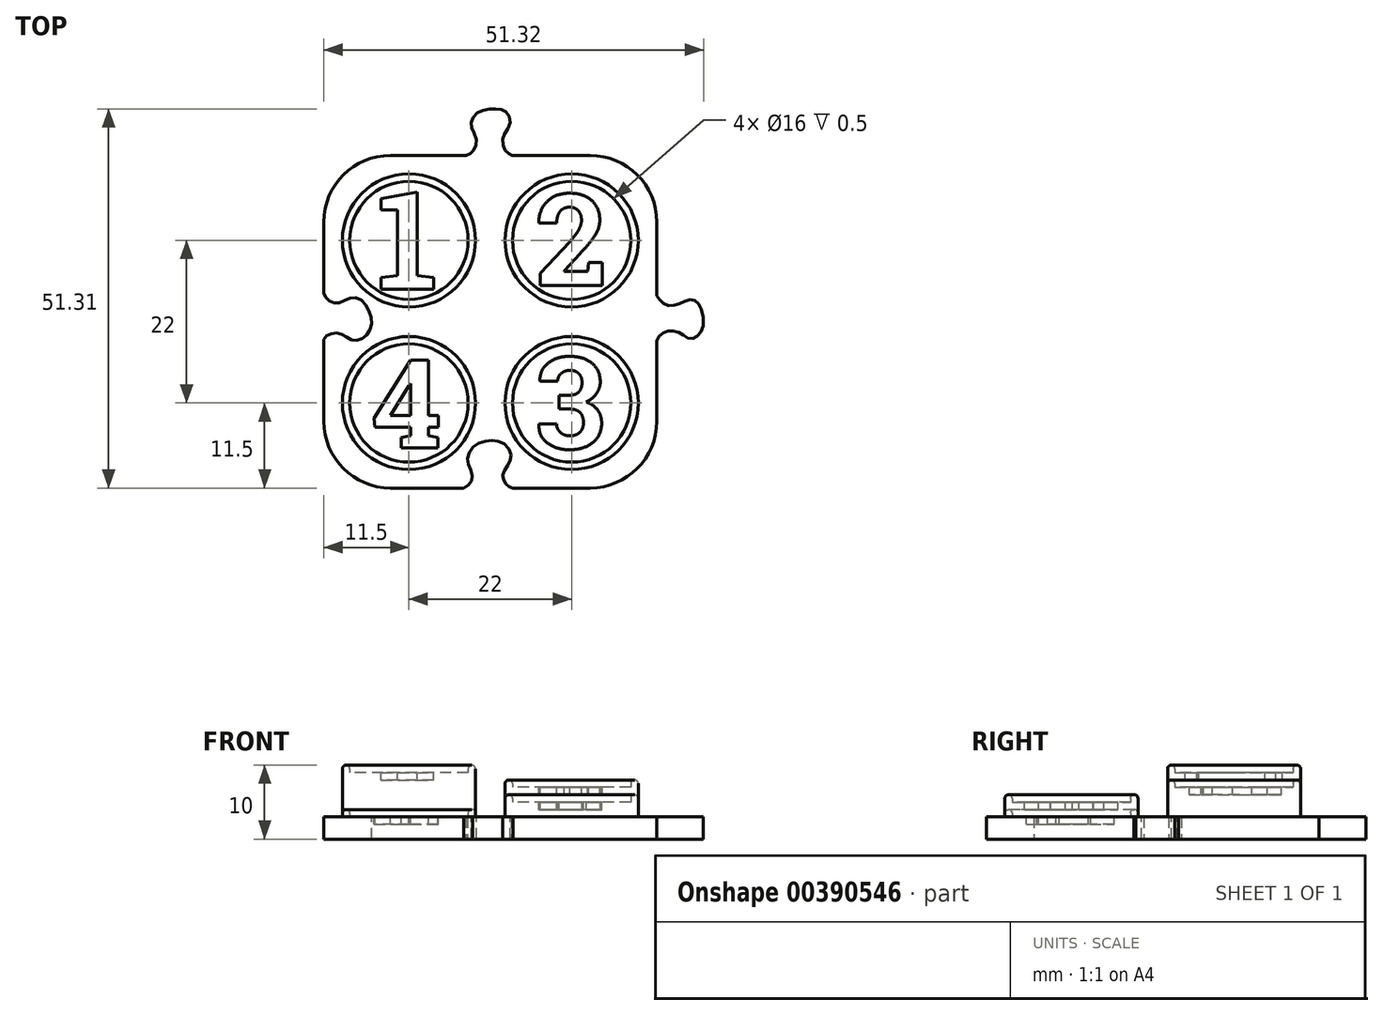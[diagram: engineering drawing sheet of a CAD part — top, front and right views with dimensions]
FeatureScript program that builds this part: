
annotation { "Feature Type Name" : "Feature", "Feature Type Description" : "" }
export const myFeature = defineFeature(function(context is Context, id is Id, definition is map)
    precondition{}
    {
        {
            var Q0;
            Q0=qCreatedBy(makeId("Top.planeOp"),FACE);
            var sketch = newSketch(context, id + "F0", { "sketchPlane" : qUnion([Q0])});
            skLineSegment(sketch, "E0.bottom", {"start": v(13.5, 13.5) * mm, "end": v(2.93, 13.5) * mm});
            skLineSegment(sketch, "E0.top", {"start": v(13.5, -13.5) * mm, "end": v(3.04, -13.5) * mm});
            skLineSegment(sketch, "E0.left", {"start": v(13.5, 13.5) * mm, "end": v(13.5, 3.49) * mm});
            skLineSegment(sketch, "E0.right", {"start": v(-13.5, 13.5) * mm, "end": v(-13.5, 3.89) * mm});
            skPoint(sketch, "E0.middle", {"position": v(0, 0) * mm});
            skFitSpline(sketch, "E1", {"points": [v(-13.5, -2.4) * mm, v(-13.06, -1.85) * mm, v(-12.19, -1.54) * mm, v(-11.23, -1.64) * mm, v(-10.18, -2.22) * mm, v(-9.3, -2.53) * mm, v(-8.23, -2.22) * mm, v(-7.52, -1.5) * mm, v(-7.03, -0.16) * mm, v(-7.37, 1.42) * mm, v(-8.21, 2.75) * mm, v(-9.3, 3.24) * mm, v(-10.53, 3) * mm, v(-11.5, 2.56) * mm, v(-12.42, 2.62) * mm, v(-13.18, 3.16) * mm, v(-13.5, 3.89) * mm], "startDerivative": vector(7.23, 11.93) * mm, "endDerivative": vector(-4.43, 14.21) * mm});
            skFitSpline(sketch, "E2", {"points": [v(-3.62, -13.5) * mm, v(-2.74, -12.9) * mm, v(-2.4, -12.05) * mm, v(-2.66, -11.08) * mm, v(-3.04, -10.02) * mm, v(-2.9, -8.8) * mm, v(-1.99, -7.67) * mm, v(-0.58, -7.14) * mm, v(0.76, -7.1) * mm, v(1.96, -7.62) * mm, v(2.79, -8.82) * mm, v(2.7, -9.8) * mm, v(2.12, -10.8) * mm, v(1.7, -11.65) * mm, v(1.76, -12.32) * mm, v(2.16, -13.02) * mm, v(2.6, -13.36) * mm, v(3.04, -13.5) * mm], "startDerivative": vector(16.2, 8.74) * mm, "endDerivative": vector(11.53, -2.8) * mm});
            skFitSpline(sketch, "E3", {"points": [v(-3.26, 13.5) * mm, v(-2.68, 13.76) * mm, v(-2.1, 14.46) * mm, v(-1.88, 15.61) * mm, v(-2.4, 17) * mm, v(-2.57, 17.9) * mm, v(-2.1, 18.93) * mm, v(-0.95, 19.6) * mm, v(0.43, 19.8) * mm, v(1.54, 19.7) * mm, v(2.37, 19.12) * mm, v(2.65, 17.8) * mm, v(2.02, 16.6) * mm, v(1.68, 15.55) * mm, v(1.92, 14.36) * mm, v(2.47, 13.75) * mm, v(2.93, 13.5) * mm], "startDerivative": vector(12.36, 4.01) * mm, "endDerivative": vector(10.48, -4.73) * mm});
            skFitSpline(sketch, "E4", {"points": [v(13.5, -2.57) * mm, v(13.97, -1.82) * mm, v(14.8, -1.34) * mm, v(15.69, -1.25) * mm, v(16.88, -1.66) * mm, v(17.63, -2.18) * mm, v(18.47, -2.24) * mm, v(19.2, -1.75) * mm, v(19.8, -0.34) * mm, v(19.4, 1.93) * mm, v(18.82, 2.75) * mm, v(18.04, 2.97) * mm, v(16.92, 2.58) * mm, v(15.97, 2.23) * mm, v(14.85, 2.24) * mm, v(13.98, 2.93) * mm, v(13.5, 3.49) * mm], "startDerivative": vector(6.76, 14.24) * mm, "endDerivative": vector(-8.43, 10.21) * mm});
            skLineSegment(sketch, "E5.trimOffspring", {"start": v(-3.26, 13.5) * mm, "end": v(-13.5, 13.5) * mm});
            skLineSegment(sketch, "E6.trimOffspring", {"start": v(13.5, -2.57) * mm, "end": v(13.5, -13.5) * mm});
            skLineSegment(sketch, "E7.trimOffspring", {"start": v(-3.62, -13.5) * mm, "end": v(-13.5, -13.5) * mm});
            skLineSegment(sketch, "E8.trimOffspring", {"start": v(-13.5, -2.4) * mm, "end": v(-13.5, -13.5) * mm});
            skPoint(sketch, "E9.visualSharp", {"position": v(-13.5, 13.5) * mm});
            skLineSegment(sketch, "E9.filletArc", {"start": v(-13.5, 13.5) * mm, "end": v(-13.5, 13.5) * mm});
            skPoint(sketch, "E10.visualSharp", {"position": v(13.5, 13.5) * mm});
            skLineSegment(sketch, "E10.filletArc", {"start": v(13.5, 13.5) * mm, "end": v(13.5, 13.5) * mm});
            skPoint(sketch, "E11.visualSharp", {"position": v(13.5, -13.5) * mm});
            skLineSegment(sketch, "E11.filletArc", {"start": v(13.5, -13.5) * mm, "end": v(13.5, -13.5) * mm});
            skPoint(sketch, "E12.visualSharp", {"position": v(-13.5, -13.5) * mm});
            skLineSegment(sketch, "E12.filletArc", {"start": v(-13.5, -13.5) * mm, "end": v(-13.5, -13.5) * mm});
            skLineSegment(sketch, "E13", {"start": v(-13.5, 4.5) * mm, "end": v(13.5, 4.5) * mm});
            skLineSegment(sketch, "E14", {"start": v(-4.5, 13.5) * mm, "end": v(-4.5, -13.5) * mm});
            skLineSegment(sketch, "E15", {"start": v(-13.5, -4.5) * mm, "end": v(13.5, -4.5) * mm});
            skLineSegment(sketch, "E16", {"start": v(4.5, 13.5) * mm, "end": v(4.5, -13.5) * mm});
            skSolve(sketch);
        }
        {
            var Q0;
            {var subQ1=sQuery(id+"F0.wireOp",EDGE,"E3");Q0=makeQuery(id+"F0.imprint","IMPRINT",FACE,{"disambiguationData":[TD([[makeQuery(id+"F0.imprint","IMPRINT",EDGE,{"derivedFrom":subQ1}),-1.0]])]});}
            var Q1;
            {var subQ0=sQuery(id+"F0.wireOp",EDGE,"E5.trimOffspring");var subQ1=sQuery(id+"F0.wireOp",EDGE,"E0.right");var subQ2=makeQuery(id+"F0.imprint","INTERSECT",VERTEX,{"derivedFrom":[subQ1,subQ0]});Q1=makeQuery(id+"F0.imprint","IMPRINT",FACE,{"disambiguationData":[TD([[makeQuery(id+"F0.imprint","IMPRINT",EDGE,{"disambiguationData":[TD([[subQ2,-1.0]])],"derivedFrom":subQ1}),1.0]])]});}
            var Q2;
            {var subQ0=sQuery(id+"F0.wireOp",EDGE,"E0.left");var subQ1=sQuery(id+"F0.wireOp",EDGE,"E0.bottom");var subQ2=makeQuery(id+"F0.imprint","INTERSECT",VERTEX,{"derivedFrom":[subQ1,subQ0]});Q2=makeQuery(id+"F0.imprint","IMPRINT",FACE,{"disambiguationData":[TD([[makeQuery(id+"F0.imprint","IMPRINT",EDGE,{"disambiguationData":[TD([[subQ2,-1.0]])],"derivedFrom":subQ1}),1.0]])]});}
            var Q3;
            {var subQ0=sQuery(id+"F0.wireOp",EDGE,"E14");var subQ1=sQuery(id+"F0.wireOp",EDGE,"E13");var subQ2=makeQuery(id+"F0.imprint","INTERSECT",VERTEX,{"derivedFrom":[subQ1,subQ0]});Q3=makeQuery(id+"F0.imprint","IMPRINT",FACE,{"disambiguationData":[TD([[makeQuery(id+"F0.imprint","IMPRINT",EDGE,{"disambiguationData":[TD([[subQ2,-1.0]])],"derivedFrom":subQ1}),-1.0]])]});}
            extrude(context, id + "F1", {"entities" : qUnion([Q0, Q1, Q2, Q3]), "depth" : 3 * mm});
        }
        {
            var Q0;
            {var subQ5=sQuery(id+"F0.wireOp",EDGE,"E4");Q0=makeQuery(id+"F0.imprint","IMPRINT",FACE,{"disambiguationData":[TD([[makeQuery(id+"F0.imprint","IMPRINT",EDGE,{"derivedFrom":subQ5}),1.0]])]});}
            var Q1;
            {var subQ0=sQuery(id+"F0.wireOp",EDGE,"E0.left");var subQ1=sQuery(id+"F0.wireOp",EDGE,"E0.bottom");var subQ2=makeQuery(id+"F0.imprint","INTERSECT",VERTEX,{"derivedFrom":[subQ1,subQ0]});Q1=makeQuery(id+"F0.imprint","IMPRINT",FACE,{"disambiguationData":[TD([[makeQuery(id+"F0.imprint","IMPRINT",EDGE,{"disambiguationData":[TD([[subQ2,-1.0]])],"derivedFrom":subQ1}),1.0]])]});}
            var Q2;
            {var subQ0=sQuery(id+"F0.wireOp",EDGE,"E6.trimOffspring");var subQ1=sQuery(id+"F0.wireOp",EDGE,"E0.top");var subQ2=makeQuery(id+"F0.imprint","INTERSECT",VERTEX,{"derivedFrom":[subQ1,subQ0]});Q2=makeQuery(id+"F0.imprint","IMPRINT",FACE,{"disambiguationData":[TD([[makeQuery(id+"F0.imprint","IMPRINT",EDGE,{"disambiguationData":[TD([[subQ2,-1.0]])],"derivedFrom":subQ1}),-1.0]])]});}
            var Q3;
            {var subQ0=sQuery(id+"F0.wireOp",EDGE,"E14");var subQ1=sQuery(id+"F0.wireOp",EDGE,"E13");var subQ2=makeQuery(id+"F0.imprint","INTERSECT",VERTEX,{"derivedFrom":[subQ1,subQ0]});Q3=makeQuery(id+"F0.imprint","IMPRINT",FACE,{"disambiguationData":[TD([[makeQuery(id+"F0.imprint","IMPRINT",EDGE,{"disambiguationData":[TD([[subQ2,-1.0]])],"derivedFrom":subQ1}),-1.0]])]});}
            extrude(context, id + "F2", {"entities" : qUnion([Q0, Q1, Q2, Q3]), "depth" : 3 * mm});
        }
        {
            var Q0;
            {var subQ5=sQuery(id+"F0.wireOp",EDGE,"E2");Q0=makeQuery(id+"F0.imprint","IMPRINT",FACE,{"disambiguationData":[TD([[makeQuery(id+"F0.imprint","IMPRINT",EDGE,{"derivedFrom":subQ5}),1.0]])]});}
            var Q1;
            {var subQ0=sQuery(id+"F0.wireOp",EDGE,"E8.trimOffspring");var subQ1=sQuery(id+"F0.wireOp",EDGE,"E7.trimOffspring");var subQ2=makeQuery(id+"F0.imprint","INTERSECT",VERTEX,{"derivedFrom":[subQ1,subQ0]});Q1=makeQuery(id+"F0.imprint","IMPRINT",FACE,{"disambiguationData":[TD([[makeQuery(id+"F0.imprint","IMPRINT",EDGE,{"disambiguationData":[TD([[subQ2,1.0]])],"derivedFrom":subQ1}),-1.0]])]});}
            var Q2;
            {var subQ0=sQuery(id+"F0.wireOp",EDGE,"E6.trimOffspring");var subQ1=sQuery(id+"F0.wireOp",EDGE,"E0.top");var subQ2=makeQuery(id+"F0.imprint","INTERSECT",VERTEX,{"derivedFrom":[subQ1,subQ0]});Q2=makeQuery(id+"F0.imprint","IMPRINT",FACE,{"disambiguationData":[TD([[makeQuery(id+"F0.imprint","IMPRINT",EDGE,{"disambiguationData":[TD([[subQ2,-1.0]])],"derivedFrom":subQ1}),-1.0]])]});}
            var Q3;
            {var subQ0=sQuery(id+"F0.wireOp",EDGE,"E14");var subQ1=sQuery(id+"F0.wireOp",EDGE,"E13");var subQ2=makeQuery(id+"F0.imprint","INTERSECT",VERTEX,{"derivedFrom":[subQ1,subQ0]});Q3=makeQuery(id+"F0.imprint","IMPRINT",FACE,{"disambiguationData":[TD([[makeQuery(id+"F0.imprint","IMPRINT",EDGE,{"disambiguationData":[TD([[subQ2,-1.0]])],"derivedFrom":subQ1}),-1.0]])]});}
            extrude(context, id + "F3", {"entities" : qUnion([Q0, Q1, Q2, Q3]), "depth" : 3 * mm});
        }
        {
            var Q0;
            {var subQ6=sQuery(id+"F0.wireOp",EDGE,"E1");Q0=makeQuery(id+"F0.imprint","IMPRINT",FACE,{"disambiguationData":[TD([[makeQuery(id+"F0.imprint","IMPRINT",EDGE,{"derivedFrom":subQ6}),-1.0]])]});}
            var Q1;
            {var subQ0=sQuery(id+"F0.wireOp",EDGE,"E5.trimOffspring");var subQ1=sQuery(id+"F0.wireOp",EDGE,"E0.right");var subQ2=makeQuery(id+"F0.imprint","INTERSECT",VERTEX,{"derivedFrom":[subQ1,subQ0]});Q1=makeQuery(id+"F0.imprint","IMPRINT",FACE,{"disambiguationData":[TD([[makeQuery(id+"F0.imprint","IMPRINT",EDGE,{"disambiguationData":[TD([[subQ2,-1.0]])],"derivedFrom":subQ1}),1.0]])]});}
            var Q2;
            {var subQ0=sQuery(id+"F0.wireOp",EDGE,"E8.trimOffspring");var subQ1=sQuery(id+"F0.wireOp",EDGE,"E7.trimOffspring");var subQ2=makeQuery(id+"F0.imprint","INTERSECT",VERTEX,{"derivedFrom":[subQ1,subQ0]});Q2=makeQuery(id+"F0.imprint","IMPRINT",FACE,{"disambiguationData":[TD([[makeQuery(id+"F0.imprint","IMPRINT",EDGE,{"disambiguationData":[TD([[subQ2,1.0]])],"derivedFrom":subQ1}),-1.0]])]});}
            var Q3;
            {var subQ0=sQuery(id+"F0.wireOp",EDGE,"E14");var subQ1=sQuery(id+"F0.wireOp",EDGE,"E13");var subQ2=makeQuery(id+"F0.imprint","INTERSECT",VERTEX,{"derivedFrom":[subQ1,subQ0]});Q3=makeQuery(id+"F0.imprint","IMPRINT",FACE,{"disambiguationData":[TD([[makeQuery(id+"F0.imprint","IMPRINT",EDGE,{"disambiguationData":[TD([[subQ2,-1.0]])],"derivedFrom":subQ1}),-1.0]])]});}
            extrude(context, id + "F4", {"entities" : qUnion([Q0, Q1, Q2, Q3]), "depth" : 3 * mm});
        }
        {
            var Q0;
            Q0=makeQuery(id+"F1.opExtrude","SWEPT_BODY",BODY,{"disambiguationData":[OSD([sQuery(id+"F0.wireOp",EDGE,"E0.bottom"),sQuery(id+"F0.wireOp",EDGE,"E0.left"),sQuery(id+"F0.wireOp",EDGE,"E0.right"),sQuery(id+"F0.wireOp",EDGE,"E3"),sQuery(id+"F0.wireOp",EDGE,"E5.trimOffspring"),sQuery(id+"F0.wireOp",EDGE,"E13"),sQuery(id+"F0.wireOp",EDGE,"E14"),sQuery(id+"F0.wireOp",EDGE,"E15"),sQuery(id+"F0.wireOp",EDGE,"E16")])]});
            transform(context, id + "F5", {"entities" : qUnion([Q0]), "transformType" : TransformType.TRANSLATION_3D, "dx" : 0 * mm, "dy" : 9 * mm, "dz" : 0 * mm, "makeCopy" : false});
        }
        {
            var Q0;
            Q0=makeQuery(id+"F2.opExtrude","SWEPT_BODY",BODY,{"disambiguationData":[OSD([sQuery(id+"F0.wireOp",EDGE,"E0.bottom"),sQuery(id+"F0.wireOp",EDGE,"E0.top"),sQuery(id+"F0.wireOp",EDGE,"E0.left"),sQuery(id+"F0.wireOp",EDGE,"E4"),sQuery(id+"F0.wireOp",EDGE,"E6.trimOffspring"),sQuery(id+"F0.wireOp",EDGE,"E13"),sQuery(id+"F0.wireOp",EDGE,"E14"),sQuery(id+"F0.wireOp",EDGE,"E15"),sQuery(id+"F0.wireOp",EDGE,"E16")])]});
            transform(context, id + "F6", {"entities" : qUnion([Q0]), "transformType" : TransformType.TRANSLATION_3D, "dx" : 9 * mm, "dy" : 0 * mm, "dz" : 0 * mm, "makeCopy" : false});
        }
        {
            var Q0;
            Q0=makeQuery(id+"F3.opExtrude","SWEPT_BODY",BODY,{"disambiguationData":[OSD([sQuery(id+"F0.wireOp",EDGE,"E0.top"),sQuery(id+"F0.wireOp",EDGE,"E2"),sQuery(id+"F0.wireOp",EDGE,"E6.trimOffspring"),sQuery(id+"F0.wireOp",EDGE,"E7.trimOffspring"),sQuery(id+"F0.wireOp",EDGE,"E8.trimOffspring"),sQuery(id+"F0.wireOp",EDGE,"E13"),sQuery(id+"F0.wireOp",EDGE,"E14"),sQuery(id+"F0.wireOp",EDGE,"E15"),sQuery(id+"F0.wireOp",EDGE,"E16")])]});
            transform(context, id + "F7", {"entities" : qUnion([Q0]), "transformType" : TransformType.TRANSLATION_3D, "dx" : 0 * mm, "dy" : -9 * mm, "dz" : 0 * mm, "makeCopy" : false});
        }
        {
            var Q0;
            Q0=makeQuery(id+"F4.opExtrude","SWEPT_BODY",BODY,{"disambiguationData":[OSD([sQuery(id+"F0.wireOp",EDGE,"E0.right"),sQuery(id+"F0.wireOp",EDGE,"E1"),sQuery(id+"F0.wireOp",EDGE,"E5.trimOffspring"),sQuery(id+"F0.wireOp",EDGE,"E7.trimOffspring"),sQuery(id+"F0.wireOp",EDGE,"E8.trimOffspring"),sQuery(id+"F0.wireOp",EDGE,"E13"),sQuery(id+"F0.wireOp",EDGE,"E14"),sQuery(id+"F0.wireOp",EDGE,"E15"),sQuery(id+"F0.wireOp",EDGE,"E16")])]});
            transform(context, id + "F8", {"entities" : qUnion([Q0]), "transformType" : TransformType.TRANSLATION_3D, "dx" : -9 * mm, "dy" : 0 * mm, "dz" : 0 * mm, "makeCopy" : false});
        }
        {
            var Q0;
            Q0=qCreatedBy(makeId("Top.planeOp"),FACE);
            var sketch = newSketch(context, id + "F9", { "sketchPlane" : qUnion([Q0])});
            skLineSegment(sketch, "E17.top", {"start": v(13.5, 22.5) * mm, "end": v(-13.5, 22.5) * mm});
            skLineSegment(sketch, "E17.left", {"start": v(22.5, -13.5) * mm, "end": v(22.5, 13.5) * mm});
            skPoint(sketch, "E18.visualSharp", {"position": v(22.5, 22.5) * mm});
            skArc(sketch, "E18.filletArc", {"start": v(22.5, 13.5) * mm, "mid": v(19.86, 19.86) * mm, "end": v(13.5, 22.5) * mm});
            skPoint(sketch, "E19.visualSharp", {"position": v(22.5, -22.5) * mm});
            skArc(sketch, "E19.filletArc", {"start": v(13.5, -22.5) * mm, "mid": v(19.86, -19.86) * mm, "end": v(22.5, -13.5) * mm});
            skPoint(sketch, "E20.visualSharp", {"position": v(-22.5, -22.5) * mm});
            skArc(sketch, "E20.filletArc", {"start": v(-22.5, -13.5) * mm, "mid": v(-19.86, -19.86) * mm, "end": v(-13.5, -22.5) * mm});
            skPoint(sketch, "E21.visualSharp", {"position": v(-22.5, 22.5) * mm});
            skArc(sketch, "E21.filletArc", {"start": v(-13.5, 22.5) * mm, "mid": v(-19.86, 19.86) * mm, "end": v(-22.5, 13.5) * mm});
            skLineSegment(sketch, "E22", {"start": v(-22.5, 13.5) * mm, "end": v(-12.08, 0) * mm});
            skLineSegment(sketch, "E23", {"start": v(-12.08, 0) * mm, "end": v(-22.5, -13.5) * mm});
            skLineSegment(sketch, "E24", {"start": v(-13.5, -22.5) * mm, "end": v(0, -11.74) * mm});
            skLineSegment(sketch, "E25", {"start": v(13.5, -22.5) * mm, "end": v(0, -11.74) * mm});
            skSolve(sketch);
        }
        {
            var Q0;
            Q0=qSketchRegion(id+"F9",true);
            extrude(context, id + "F10", {"entities" : qUnion([Q0]), "depth" : 3 * mm});
        }
        {
            var Q0;
            Q0=makeQuery(id+"F1.opExtrude","SWEPT_BODY",BODY,{"disambiguationData":[OSD([sQuery(id+"F0.wireOp",EDGE,"E0.bottom"),sQuery(id+"F0.wireOp",EDGE,"E0.left"),sQuery(id+"F0.wireOp",EDGE,"E0.right"),sQuery(id+"F0.wireOp",EDGE,"E3"),sQuery(id+"F0.wireOp",EDGE,"E5.trimOffspring"),sQuery(id+"F0.wireOp",EDGE,"E13"),sQuery(id+"F0.wireOp",EDGE,"E14"),sQuery(id+"F0.wireOp",EDGE,"E15"),sQuery(id+"F0.wireOp",EDGE,"E16")])]});
            var Q1;
            Q1=makeQuery(id+"F2.opExtrude","SWEPT_BODY",BODY,{"disambiguationData":[OSD([sQuery(id+"F0.wireOp",EDGE,"E0.bottom"),sQuery(id+"F0.wireOp",EDGE,"E0.top"),sQuery(id+"F0.wireOp",EDGE,"E0.left"),sQuery(id+"F0.wireOp",EDGE,"E4"),sQuery(id+"F0.wireOp",EDGE,"E6.trimOffspring"),sQuery(id+"F0.wireOp",EDGE,"E13"),sQuery(id+"F0.wireOp",EDGE,"E14"),sQuery(id+"F0.wireOp",EDGE,"E15"),sQuery(id+"F0.wireOp",EDGE,"E16")])]});
            var Q2;
            Q2=makeQuery(id+"F3.opExtrude","SWEPT_BODY",BODY,{"disambiguationData":[OSD([sQuery(id+"F0.wireOp",EDGE,"E0.top"),sQuery(id+"F0.wireOp",EDGE,"E2"),sQuery(id+"F0.wireOp",EDGE,"E6.trimOffspring"),sQuery(id+"F0.wireOp",EDGE,"E7.trimOffspring"),sQuery(id+"F0.wireOp",EDGE,"E8.trimOffspring"),sQuery(id+"F0.wireOp",EDGE,"E13"),sQuery(id+"F0.wireOp",EDGE,"E14"),sQuery(id+"F0.wireOp",EDGE,"E15"),sQuery(id+"F0.wireOp",EDGE,"E16")])]});
            var Q3;
            Q3=makeQuery(id+"F4.opExtrude","SWEPT_BODY",BODY,{"disambiguationData":[OSD([sQuery(id+"F0.wireOp",EDGE,"E0.right"),sQuery(id+"F0.wireOp",EDGE,"E1"),sQuery(id+"F0.wireOp",EDGE,"E5.trimOffspring"),sQuery(id+"F0.wireOp",EDGE,"E7.trimOffspring"),sQuery(id+"F0.wireOp",EDGE,"E8.trimOffspring"),sQuery(id+"F0.wireOp",EDGE,"E13"),sQuery(id+"F0.wireOp",EDGE,"E14"),sQuery(id+"F0.wireOp",EDGE,"E15"),sQuery(id+"F0.wireOp",EDGE,"E16")])]});
            var Q4;
            Q4=makeQuery(id+"F10.opExtrude","SWEPT_BODY",BODY,{"disambiguationData":[OSD([sQuery(id+"F9.wireOp",EDGE,"E17.top"),sQuery(id+"F9.wireOp",EDGE,"E17.left"),sQuery(id+"F9.wireOp",EDGE,"E18.filletArc"),sQuery(id+"F9.wireOp",EDGE,"E19.filletArc"),sQuery(id+"F9.wireOp",EDGE,"E20.filletArc"),sQuery(id+"F9.wireOp",EDGE,"E21.filletArc"),sQuery(id+"F9.wireOp",EDGE,"E22"),sQuery(id+"F9.wireOp",EDGE,"E23"),sQuery(id+"F9.wireOp",EDGE,"E24"),sQuery(id+"F9.wireOp",EDGE,"E25")])]});
            booleanBodies(context, id + "F11", {"operationType" : BooleanOperationType.UNION, "tools" : qUnion([Q0, Q1, Q2, Q3, Q4])});
        }
        {
            var Q0;
            {var subQ0=sQuery(id+"F0.wireOp",EDGE,"E16");var subQ1=sQuery(id+"F0.wireOp",EDGE,"E15");var subQ2=sQuery(id+"F0.wireOp",EDGE,"E14");var subQ3=sQuery(id+"F0.wireOp",EDGE,"E13");var subQ4=sQuery(id+"F0.wireOp",EDGE,"E8.trimOffspring");var subQ5=sQuery(id+"F0.wireOp",EDGE,"E7.trimOffspring");var subQ6=sQuery(id+"F0.wireOp",EDGE,"E5.trimOffspring");var subQ7=sQuery(id+"F0.wireOp",EDGE,"E0.right");var subQ8=sQuery(id+"F0.wireOp",EDGE,"E6.trimOffspring");var subQ9=sQuery(id+"F0.wireOp",EDGE,"E0.top");var subQ10=sQuery(id+"F0.wireOp",EDGE,"E0.left");var subQ11=sQuery(id+"F0.wireOp",EDGE,"E0.bottom");Q0=makeQuery(id+"F11.opBoolean","MERGE",FACE,{"derivedFrom":[makeQuery(id+"F1.opExtrude","CAP_FACE",FACE,{"disambiguationData":[OSD([subQ11,subQ10,subQ7,sQuery(id+"F0.wireOp",EDGE,"E3"),subQ6,subQ3,subQ2,subQ1,subQ0])],"isStart":false}),makeQuery(id+"F2.opExtrude","CAP_FACE",FACE,{"disambiguationData":[OSD([subQ11,subQ9,subQ10,sQuery(id+"F0.wireOp",EDGE,"E4"),subQ8,subQ3,subQ2,subQ1,subQ0])],"isStart":false}),makeQuery(id+"F3.opExtrude","CAP_FACE",FACE,{"disambiguationData":[OSD([subQ9,sQuery(id+"F0.wireOp",EDGE,"E2"),subQ8,subQ5,subQ4,subQ3,subQ2,subQ1,subQ0])],"isStart":false}),makeQuery(id+"F4.opExtrude","CAP_FACE",FACE,{"disambiguationData":[OSD([subQ7,sQuery(id+"F0.wireOp",EDGE,"E1"),subQ6,subQ5,subQ4,subQ3,subQ2,subQ1,subQ0])],"isStart":false}),makeQuery(id+"F10.opExtrude","CAP_FACE",FACE,{"disambiguationData":[OSD([sQuery(id+"F9.wireOp",EDGE,"E17.top"),sQuery(id+"F9.wireOp",EDGE,"E17.left"),sQuery(id+"F9.wireOp",EDGE,"E18.filletArc"),sQuery(id+"F9.wireOp",EDGE,"E19.filletArc"),sQuery(id+"F9.wireOp",EDGE,"E20.filletArc"),sQuery(id+"F9.wireOp",EDGE,"E21.filletArc"),sQuery(id+"F9.wireOp",EDGE,"E22"),sQuery(id+"F9.wireOp",EDGE,"E23"),sQuery(id+"F9.wireOp",EDGE,"E24"),sQuery(id+"F9.wireOp",EDGE,"E25")])],"isStart":false})]});}
            var sketch = newSketch(context, id + "F12", { "sketchPlane" : qUnion([Q0])});
            skLineSegment(sketch, "E26.bottom", {"start": v(11, -11) * mm, "end": v(-11, -11) * mm, "construction": true});
            skLineSegment(sketch, "E26.top", {"start": v(11, 11) * mm, "end": v(-11, 11) * mm, "construction": true});
            skLineSegment(sketch, "E26.left", {"start": v(11, -11) * mm, "end": v(11, 11) * mm, "construction": true});
            skLineSegment(sketch, "E26.right", {"start": v(-11, -11) * mm, "end": v(-11, 11) * mm, "construction": true});
            skPoint(sketch, "E26.middle", {"position": v(0, 0) * mm});
            skCircle(sketch, "E27", {"center": v(-11, 11) * mm, "radius": 9 * mm});
            skCircle(sketch, "E28", {"center": v(11, 11) * mm, "radius": 9 * mm});
            skCircle(sketch, "E29", {"center": v(11, -11) * mm, "radius": 9 * mm});
            skCircle(sketch, "E30", {"center": v(-11, -11) * mm, "radius": 9 * mm});
            skCircle(sketch, "E31", {"center": v(-11, 11) * mm, "radius": 8 * mm});
            skCircle(sketch, "E32", {"center": v(11, 11) * mm, "radius": 8 * mm});
            skCircle(sketch, "E33", {"center": v(11, -11) * mm, "radius": 8 * mm});
            skCircle(sketch, "E34", {"center": v(-11, -11) * mm, "radius": 8 * mm});
            skSolve(sketch);
        }
        {
            var Q0;
            Q0=makeQuery(id+"F12.imprint","IMPRINT",FACE,{"disambiguationData":[TD([[makeQuery(id+"F12.imprint","IMPRINT",EDGE,{"derivedFrom":sQuery(id+"F12.wireOp",EDGE,"E27")}),1.0]])]});
            extrude(context, id + "F13", {"entities" : qUnion([Q0]), "operationType" : NewBodyOperationType.ADD, "depth" : 7 * mm});
        }
        {
            var Q0;
            {var subQ0=sQuery(id+"F0.wireOp",EDGE,"E16");var subQ1=sQuery(id+"F0.wireOp",EDGE,"E15");var subQ2=sQuery(id+"F0.wireOp",EDGE,"E14");var subQ3=sQuery(id+"F0.wireOp",EDGE,"E13");var subQ4=sQuery(id+"F0.wireOp",EDGE,"E8.trimOffspring");var subQ5=sQuery(id+"F0.wireOp",EDGE,"E7.trimOffspring");var subQ6=sQuery(id+"F0.wireOp",EDGE,"E5.trimOffspring");var subQ7=sQuery(id+"F0.wireOp",EDGE,"E0.right");var subQ8=sQuery(id+"F0.wireOp",EDGE,"E6.trimOffspring");var subQ9=sQuery(id+"F0.wireOp",EDGE,"E0.top");var subQ10=sQuery(id+"F0.wireOp",EDGE,"E0.left");var subQ11=sQuery(id+"F0.wireOp",EDGE,"E0.bottom");Q0=makeQuery(id+"F13.boolean.opBoolean","SPLIT",FACE,{"disambiguationData":[TD([makeQuery(id+"F13.opExtrude","SWEPT_FACE",FACE,{"disambiguationData":[OSD([sQuery(id+"F12.wireOp",EDGE,"E31")])]})])],"derivedFrom":makeQuery(id+"F11.opBoolean","MERGE",FACE,{"derivedFrom":[makeQuery(id+"F1.opExtrude","CAP_FACE",FACE,{"disambiguationData":[OSD([subQ11,subQ10,subQ7,sQuery(id+"F0.wireOp",EDGE,"E3"),subQ6,subQ3,subQ2,subQ1,subQ0])],"isStart":false}),makeQuery(id+"F2.opExtrude","CAP_FACE",FACE,{"disambiguationData":[OSD([subQ11,subQ9,subQ10,sQuery(id+"F0.wireOp",EDGE,"E4"),subQ8,subQ3,subQ2,subQ1,subQ0])],"isStart":false}),makeQuery(id+"F3.opExtrude","CAP_FACE",FACE,{"disambiguationData":[OSD([subQ9,sQuery(id+"F0.wireOp",EDGE,"E2"),subQ8,subQ5,subQ4,subQ3,subQ2,subQ1,subQ0])],"isStart":false}),makeQuery(id+"F4.opExtrude","CAP_FACE",FACE,{"disambiguationData":[OSD([subQ7,sQuery(id+"F0.wireOp",EDGE,"E1"),subQ6,subQ5,subQ4,subQ3,subQ2,subQ1,subQ0])],"isStart":false}),makeQuery(id+"F10.opExtrude","CAP_FACE",FACE,{"disambiguationData":[OSD([sQuery(id+"F9.wireOp",EDGE,"E17.top"),sQuery(id+"F9.wireOp",EDGE,"E17.left"),sQuery(id+"F9.wireOp",EDGE,"E18.filletArc"),sQuery(id+"F9.wireOp",EDGE,"E19.filletArc"),sQuery(id+"F9.wireOp",EDGE,"E20.filletArc"),sQuery(id+"F9.wireOp",EDGE,"E21.filletArc"),sQuery(id+"F9.wireOp",EDGE,"E22"),sQuery(id+"F9.wireOp",EDGE,"E23"),sQuery(id+"F9.wireOp",EDGE,"E24"),sQuery(id+"F9.wireOp",EDGE,"E25")])],"isStart":false})]})});}
            extrude(context, id + "F14", {"entities" : qUnion([Q0]), "operationType" : NewBodyOperationType.ADD, "depth" : 6 * mm});
        }
        {
            var Q0;
            Q0=makeQuery(id+"F12.imprint","IMPRINT",FACE,{"disambiguationData":[TD([[makeQuery(id+"F12.imprint","IMPRINT",EDGE,{"derivedFrom":sQuery(id+"F12.wireOp",EDGE,"E28")}),1.0]])]});
            extrude(context, id + "F15", {"entities" : qUnion([Q0]), "operationType" : NewBodyOperationType.ADD, "depth" : 5 * mm});
        }
        {
            var Q0;
            Q0=makeQuery(id+"F12.imprint","IMPRINT",FACE,{"disambiguationData":[TD([[makeQuery(id+"F12.imprint","IMPRINT",EDGE,{"derivedFrom":sQuery(id+"F12.wireOp",EDGE,"E32")}),1.0]])]});
            extrude(context, id + "F16", {"entities" : qUnion([Q0]), "operationType" : NewBodyOperationType.ADD, "depth" : 4 * mm});
        }
        {
            var Q0;
            Q0=makeQuery(id+"F12.imprint","IMPRINT",FACE,{"disambiguationData":[TD([[makeQuery(id+"F12.imprint","IMPRINT",EDGE,{"derivedFrom":sQuery(id+"F12.wireOp",EDGE,"E29")}),1.0]])]});
            extrude(context, id + "F17", {"entities" : qUnion([Q0]), "operationType" : NewBodyOperationType.ADD, "depth" : 3 * mm});
        }
        {
            var Q0;
            Q0=makeQuery(id+"F12.imprint","IMPRINT",FACE,{"disambiguationData":[TD([[makeQuery(id+"F12.imprint","IMPRINT",EDGE,{"derivedFrom":sQuery(id+"F12.wireOp",EDGE,"E33")}),1.0]])]});
            extrude(context, id + "F18", {"entities" : qUnion([Q0]), "operationType" : NewBodyOperationType.ADD, "depth" : 2 * mm});
        }
        {
            var Q0;
            Q0=makeQuery(id+"F12.imprint","IMPRINT",FACE,{"disambiguationData":[TD([[makeQuery(id+"F12.imprint","IMPRINT",EDGE,{"derivedFrom":sQuery(id+"F12.wireOp",EDGE,"E30")}),1.0]])]});
            extrude(context, id + "F19", {"entities" : qUnion([Q0]), "operationType" : NewBodyOperationType.ADD, "depth" : 1 * mm});
        }
        {
            var Q0;
            Q0=makeQuery(id+"F14.opExtrude","CAP_FACE",FACE,{"disambiguationData":[OSD([sQuery(id+"F0.wireOp",EDGE,"E0.bottom"),sQuery(id+"F0.wireOp",EDGE,"E0.top"),sQuery(id+"F0.wireOp",EDGE,"E0.left"),sQuery(id+"F0.wireOp",EDGE,"E0.right"),sQuery(id+"F0.wireOp",EDGE,"E1"),sQuery(id+"F0.wireOp",EDGE,"E2"),sQuery(id+"F0.wireOp",EDGE,"E3"),sQuery(id+"F0.wireOp",EDGE,"E4"),sQuery(id+"F0.wireOp",EDGE,"E5.trimOffspring"),sQuery(id+"F0.wireOp",EDGE,"E6.trimOffspring"),sQuery(id+"F0.wireOp",EDGE,"E7.trimOffspring"),sQuery(id+"F0.wireOp",EDGE,"E8.trimOffspring"),sQuery(id+"F0.wireOp",EDGE,"E13"),sQuery(id+"F0.wireOp",EDGE,"E14"),sQuery(id+"F0.wireOp",EDGE,"E15"),sQuery(id+"F0.wireOp",EDGE,"E16"),sQuery(id+"F9.wireOp",EDGE,"E17.top"),sQuery(id+"F9.wireOp",EDGE,"E17.left"),sQuery(id+"F9.wireOp",EDGE,"E18.filletArc"),sQuery(id+"F9.wireOp",EDGE,"E19.filletArc"),sQuery(id+"F9.wireOp",EDGE,"E20.filletArc"),sQuery(id+"F9.wireOp",EDGE,"E21.filletArc"),sQuery(id+"F9.wireOp",EDGE,"E22"),sQuery(id+"F9.wireOp",EDGE,"E23"),sQuery(id+"F9.wireOp",EDGE,"E24"),sQuery(id+"F9.wireOp",EDGE,"E25")])],"isStart":false});
            var sketch = newSketch(context, id + "F20", { "sketchPlane" : qUnion([Q0])});
            skText(sketch, "E35", { "text": "1", "fontName": "RobotoSlab-Bold.ttf"});
            const initialGuessF20  = {"E35": [-0.01534, 0.00437, 1, 0, 0.01335]};
            skSetInitialGuess(sketch, initialGuessF20);
            skSolve(sketch);
        }
        {
            var Q0;
            Q0=makeQuery(id+"F16.opExtrude","CAP_FACE",FACE,{"disambiguationData":[OSD([sQuery(id+"F12.wireOp",EDGE,"E32")])],"isStart":false});
            var sketch = newSketch(context, id + "F21", { "sketchPlane" : qUnion([Q0])});
            skText(sketch, "E36", { "text": "2", "fontName": "RobotoSlab-Bold.ttf"});
            const initialGuessF21  = {"E36": [0.00615, 0.00493, 1, 0, 0.01244]};
            skSetInitialGuess(sketch, initialGuessF21);
            skSolve(sketch);
        }
        {
            var Q0;
            Q0=makeQuery(id+"F12.imprint","IMPRINT",FACE,{"disambiguationData":[TD([[makeQuery(id+"F12.imprint","IMPRINT",EDGE,{"derivedFrom":sQuery(id+"F12.wireOp",EDGE,"E34")}),1.0]])]});
            var sketch = newSketch(context, id + "F22", { "sketchPlane" : qUnion([Q0])});
            skText(sketch, "E37", { "text": "4", "fontName": "RobotoSlab-Bold.ttf"});
            const initialGuessF22  = {"E37": [-0.01602, -0.0171, 1, 0, 0.01205]};
            skSetInitialGuess(sketch, initialGuessF22);
            skSolve(sketch);
        }
        {
            var Q0;
            Q0=makeQuery(id+"F18.opExtrude","CAP_FACE",FACE,{"disambiguationData":[OSD([sQuery(id+"F12.wireOp",EDGE,"E33")])],"isStart":false});
            var sketch = newSketch(context, id + "F23", { "sketchPlane" : qUnion([Q0])});
            skText(sketch, "E38", { "text": "3", "fontName": "RobotoSlab-Bold.ttf"});
            const initialGuessF23  = {"E38": [0.00607, -0.01715, 1, 0, 0.01245]};
            skSetInitialGuess(sketch, initialGuessF23);
            skSolve(sketch);
        }
        {
            var Q0;
            Q0 = qSketchRegion(id + "F20", true);
            extrude(context, id + "F24", {"entities" : qUnion([Q0]), "operationType" : NewBodyOperationType.REMOVE, "oppositeDirection" : true, "depth" : 1 * mm});
        }
        {
            var Q0;
            Q0=makeQuery(id+"F21.imprint","IMPRINT",FACE,{"disambiguationData":[TD([[makeQuery(id+"F21.imprint","IMPRINT",EDGE,{"derivedFrom":sQuery(id+"F21.wireOp",EDGE,"E36.sketch_text.stroke-0")}),-1.0]])]});
            extrude(context, id + "F25", {"entities" : qUnion([Q0]), "operationType" : NewBodyOperationType.REMOVE, "oppositeDirection" : true, "depth" : 1 * mm});
        }
        {
            var Q0;
            Q0 = qSketchRegion(id + "F23", true);
            extrude(context, id + "F26", {"entities" : qUnion([Q0]), "operationType" : NewBodyOperationType.REMOVE, "oppositeDirection" : true, "depth" : 1 * mm});
        }
        {
            var Q0;
            Q0=makeQuery(id+"F22.imprint","IMPRINT",FACE,{"disambiguationData":[TD([[makeQuery(id+"F22.imprint","IMPRINT",EDGE,{"derivedFrom":sQuery(id+"F22.wireOp",EDGE,"E37.sketch_text.stroke-0")}),-1.0]])]});
            extrude(context, id + "F27", {"entities" : qUnion([Q0]), "operationType" : NewBodyOperationType.REMOVE, "oppositeDirection" : true, "depth" : 1 * mm});
        }
        {
            var Q0;
            Q0=makeQuery(id+"F13.opExtrude","CAP_FACE",FACE,{"disambiguationData":[OSD([sQuery(id+"F12.wireOp",EDGE,"E27"),sQuery(id+"F12.wireOp",EDGE,"E31")])],"isStart":false});
            fillet(context, id + "F28", {"entities" : qUnion([Q0]), "radius" : 0.5 * mm, "tangentPropagation" : true, "allowEdgeOverflow" : false});
        }
        {
            var Q0;
            Q0=makeQuery(id+"F15.opExtrude","CAP_FACE",FACE,{"disambiguationData":[OSD([sQuery(id+"F12.wireOp",EDGE,"E28"),sQuery(id+"F12.wireOp",EDGE,"E32")])],"isStart":false});
            fillet(context, id + "F29", {"entities" : qUnion([Q0]), "radius" : 0.5 * mm, "tangentPropagation" : true, "allowEdgeOverflow" : false});
        }
        {
            var Q0;
            Q0=makeQuery(id+"F17.opExtrude","CAP_FACE",FACE,{"disambiguationData":[OSD([sQuery(id+"F12.wireOp",EDGE,"E29"),sQuery(id+"F12.wireOp",EDGE,"E33")])],"isStart":false});
            fillet(context, id + "F30", {"entities" : qUnion([Q0]), "radius" : 0.5 * mm, "tangentPropagation" : true, "allowEdgeOverflow" : false});
        }
        {
            var Q0;
            Q0=makeQuery(id+"F19.opExtrude","CAP_FACE",FACE,{"disambiguationData":[OSD([sQuery(id+"F12.wireOp",EDGE,"E30"),sQuery(id+"F12.wireOp",EDGE,"E34")])],"isStart":false});
            fillet(context, id + "F31", {"entities" : qUnion([Q0]), "radius" : 0.5 * mm, "tangentPropagation" : true, "allowEdgeOverflow" : false});
        }
    });
